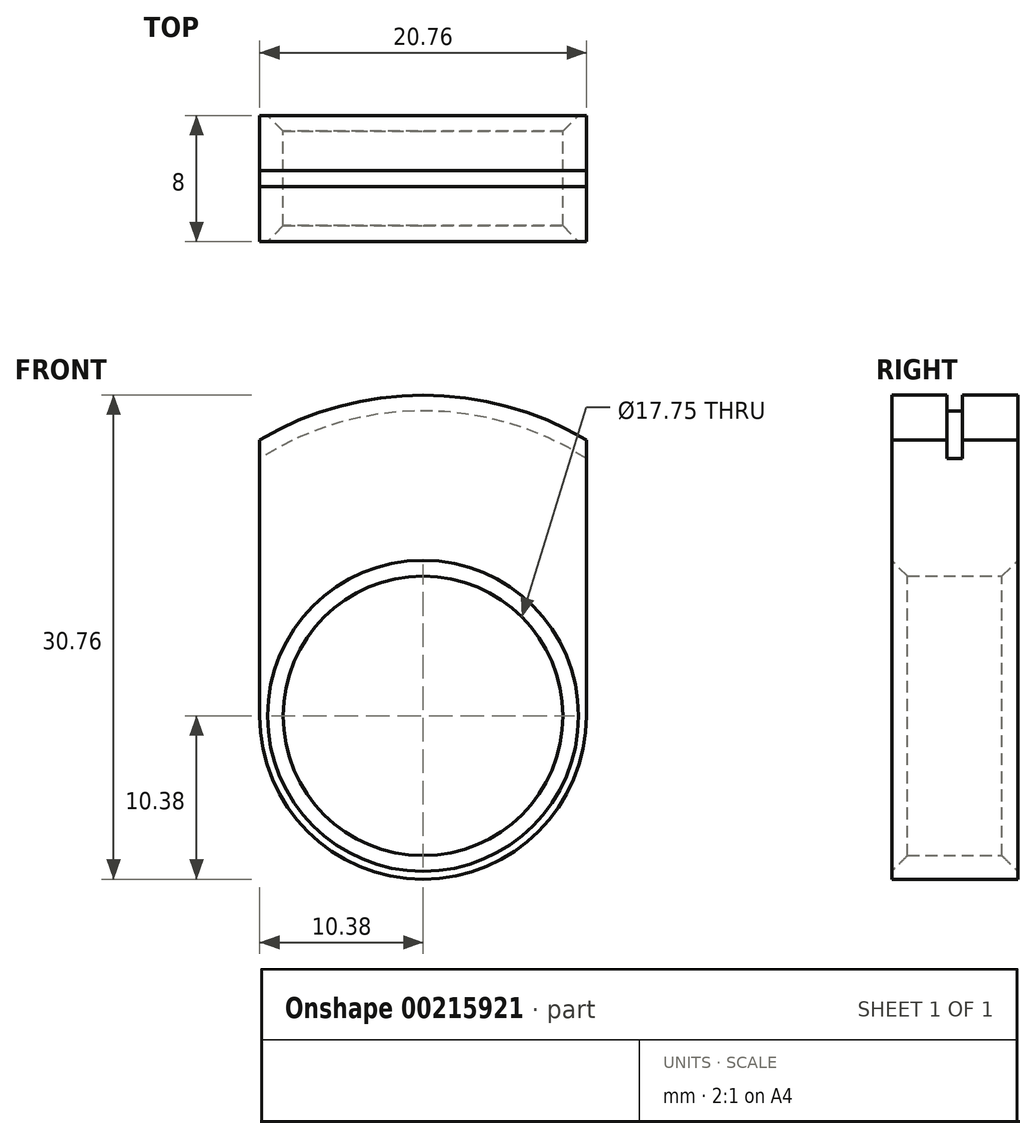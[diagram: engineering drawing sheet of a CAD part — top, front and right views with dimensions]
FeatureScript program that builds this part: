
annotation { "Feature Type Name" : "Feature", "Feature Type Description" : "" }
export const myFeature = defineFeature(function(context is Context, id is Id, definition is map)
    precondition{}
    {
        {
            var Q0;
            Q0=qCreatedBy(makeId("Front.planeOp"),FACE);
            var sketch = newSketch(context, id + "F0", { "sketchPlane" : qUnion([Q0])});
            skCircle(sketch, "E0", {"center": v(0, 0) * mm, "radius": 8.88 * mm});
            skCircle(sketch, "E1.0", {"center": v(0, 0) * mm, "radius": 10.38 * mm});
            skCircle(sketch, "E2.0", {"center": v(0, 0) * mm, "radius": 20.38 * mm});
            skLineSegment(sketch, "E3", {"start": v(10.38, 0) * mm, "end": v(10.38, 17.54) * mm});
            skLineSegment(sketch, "E4.MirrorCS", {"start": v(-10.38, 0) * mm, "end": v(-10.38, 17.54) * mm});
            skCircle(sketch, "E5.0", {"center": v(0, 0) * mm, "radius": 19.38 * mm});
            skSolve(sketch);
        }
        {
            var Q0;
            Q0=makeQuery(id+"F0.imprint","IMPRINT",FACE,{"disambiguationData":[TD([[makeQuery(id+"F0.imprint","IMPRINT",EDGE,{"derivedFrom":sQuery(id+"F0.wireOp",EDGE,"E0")}),-1.0]])]});
            extrude(context, id + "F1", {"entities" : qUnion([Q0]), "depth" : 4 * mm, "hasSecondDirection" : true, "secondDirectionOppositeDirection" : true, "secondDirectionDepth" : 4 * mm});
        }
        {
            var Q0;
            Q0=makeQuery(id+"F1.opExtrude","CAP_EDGE",EDGE,{"disambiguationData":[OSD([sQuery(id+"F0.wireOp",EDGE,"E0")])],"isStart":false});
            var Q1;
            Q1=makeQuery(id+"F1.opExtrude","CAP_EDGE",EDGE,{"disambiguationData":[OSD([sQuery(id+"F0.wireOp",EDGE,"E0")])],"isStart":true});
            chamfer(context, id + "F2", {"entities" : qUnion([Q0, Q1]), "width" : 1 * mm, "tangentPropagation" : true});
        }
        {
            var Q0;
            {var subQ0=sQuery(id+"F0.wireOp",EDGE,"E3");var subQ1=sQuery(id+"F0.wireOp",EDGE,"E1.0");var subQ2=makeQuery(id+"F0.imprint","INTERSECT",VERTEX,{"derivedFrom":[subQ1,subQ0]});Q0=makeQuery(id+"F0.imprint","IMPRINT",FACE,{"disambiguationData":[TD([[makeQuery(id+"F0.imprint","IMPRINT",EDGE,{"disambiguationData":[TD([[subQ2,-1.0]])],"derivedFrom":subQ1}),-1.0]])]});}
            var Q1;
            {var subQ0=sQuery(id+"F0.wireOp",EDGE,"E3");var subQ1=sQuery(id+"F0.wireOp",EDGE,"E2.0");var subQ2=makeQuery(id+"F0.imprint","INTERSECT",VERTEX,{"derivedFrom":[subQ1,subQ0]});Q1=makeQuery(id+"F0.imprint","IMPRINT",FACE,{"disambiguationData":[TD([[makeQuery(id+"F0.imprint","IMPRINT",EDGE,{"disambiguationData":[TD([[subQ2,-1.0]])],"derivedFrom":subQ1}),1.0]])]});}
            extrude(context, id + "F3", {"entities" : qUnion([Q0, Q1]), "operationType" : NewBodyOperationType.ADD, "depth" : 4 * mm, "hasSecondDirection" : true, "secondDirectionOppositeDirection" : true, "secondDirectionDepth" : 4 * mm});
        }
        {
            var Q0;
            {var subQ0=sQuery(id+"F0.wireOp",EDGE,"E3");var subQ1=sQuery(id+"F0.wireOp",EDGE,"E2.0");var subQ2=makeQuery(id+"F0.imprint","INTERSECT",VERTEX,{"derivedFrom":[subQ1,subQ0]});Q0=makeQuery(id+"F0.imprint","IMPRINT",FACE,{"disambiguationData":[TD([[makeQuery(id+"F0.imprint","IMPRINT",EDGE,{"disambiguationData":[TD([[subQ2,-1.0]])],"derivedFrom":subQ1}),1.0]])]});}
            extrude(context, id + "F4", {"entities" : qUnion([Q0]), "operationType" : NewBodyOperationType.REMOVE, "oppositeDirection" : true, "depth" : .5 * mm, "hasSecondDirection" : true, "secondDirectionOppositeDirection" : false, "secondDirectionDepth" : .5 * mm});
        }
    });
